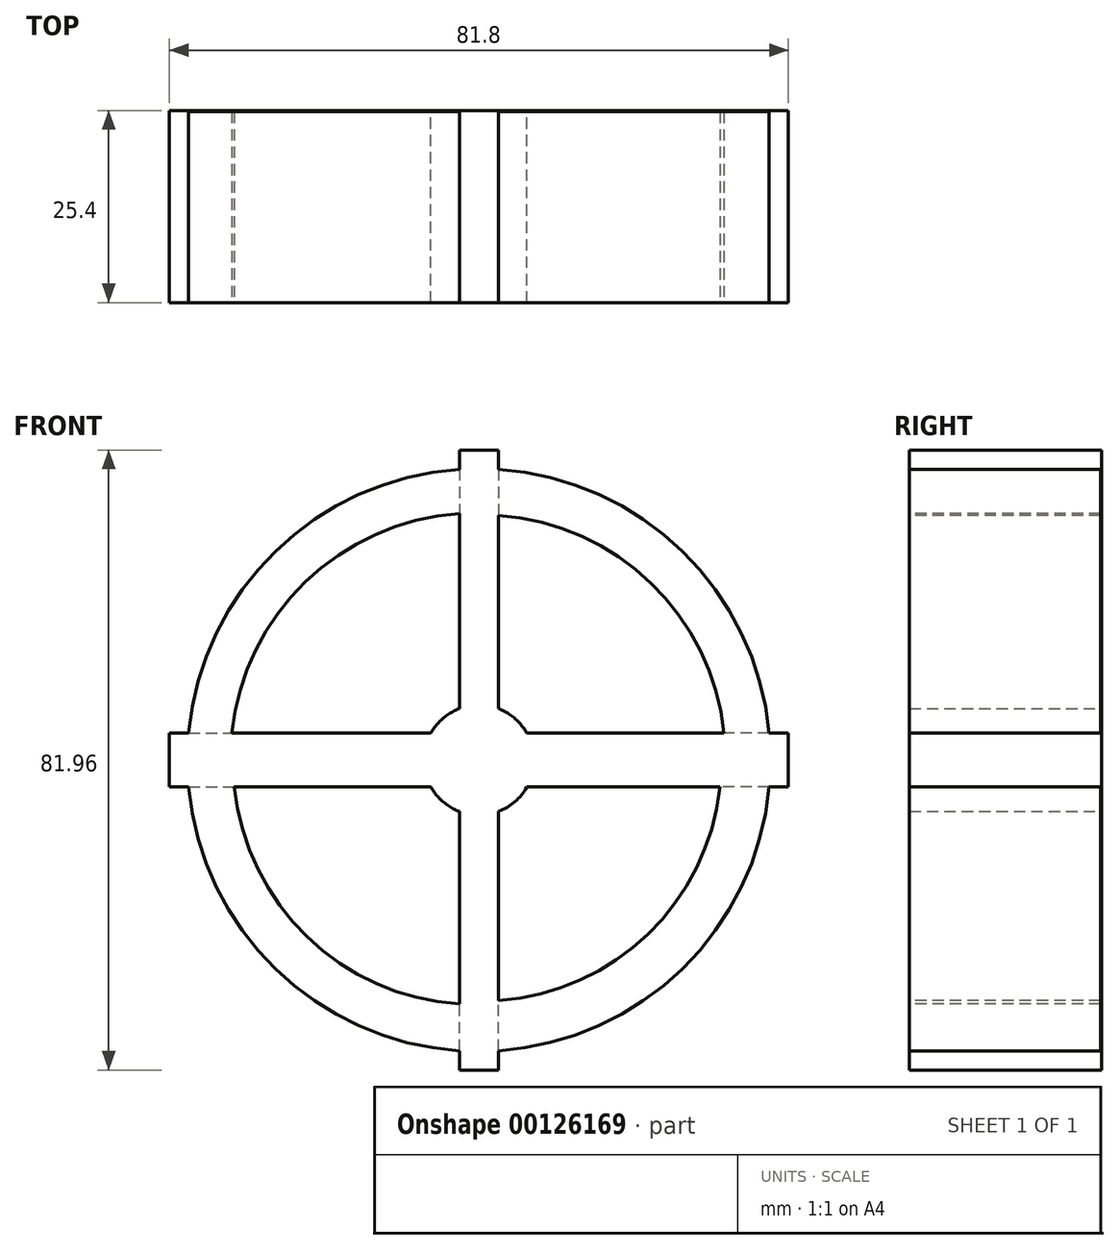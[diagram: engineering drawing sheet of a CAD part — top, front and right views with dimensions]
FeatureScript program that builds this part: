
annotation { "Feature Type Name" : "Feature", "Feature Type Description" : "" }
export const myFeature = defineFeature(function(context is Context, id is Id, definition is map)
    precondition{}
    {
        {
            var Q0;
            Q0=qCreatedBy(makeId("Front.planeOp"),FACE);
            var sketch = newSketch(context, id + "F0", { "sketchPlane" : qUnion([Q0])});
            skLineSegment(sketch, "E0", {"start": v(-2.58, -40.98) * mm, "end": v(-2.58, -40.98) * mm});
            skArc(sketch, "E1", {"start": v(-6.34, -3.57) * mm, "mid": v(-4.74, -5.52) * mm, "end": v(-2.58, -6.8) * mm});
            skLineSegment(sketch, "E2", {"start": v(-2.58, 40.98) * mm, "end": v(-2.58, 6.8) * mm});
            skLineSegment(sketch, "E3.MirrorCS", {"start": v(2.58, 40.98) * mm, "end": v(2.58, 6.8) * mm});
            skLineSegment(sketch, "E4.MirrorCS", {"start": v(-2.58, -40.98) * mm, "end": v(-2.58, -6.8) * mm});
            skLineSegment(sketch, "E5.MirrorCS", {"start": v(2.58, -40.98) * mm, "end": v(2.58, -6.8) * mm});
            skLineSegment(sketch, "E6", {"start": v(-40.9, -3.57) * mm, "end": v(-6.34, -3.57) * mm});
            skLineSegment(sketch, "E7.MirrorCS", {"start": v(-40.9, 3.57) * mm, "end": v(-6.34, 3.57) * mm});
            skLineSegment(sketch, "E8.MirrorCS", {"start": v(40.9, 3.57) * mm, "end": v(6.34, 3.57) * mm});
            skLineSegment(sketch, "E9.MirrorCS", {"start": v(40.9, -3.57) * mm, "end": v(6.34, -3.57) * mm});
            skLineSegment(sketch, "E10.left", {"start": v(-40.9, 3.57) * mm, "end": v(-40.9, -3.57) * mm});
            skLineSegment(sketch, "E10.right", {"start": v(-6.34, 3.57) * mm, "end": v(-6.34, -3.57) * mm});
            skLineSegment(sketch, "E11.bottom", {"start": v(-2.58, 40.98) * mm, "end": v(2.58, 40.98) * mm});
            skLineSegment(sketch, "E11.top", {"start": v(-2.58, 40.98) * mm, "end": v(2.58, 40.98) * mm});
            skLineSegment(sketch, "E11.left", {"start": v(-2.58, 40.98) * mm, "end": v(-2.58, 40.98) * mm});
            skLineSegment(sketch, "E11.right", {"start": v(2.58, 40.98) * mm, "end": v(2.58, 40.98) * mm});
            skLineSegment(sketch, "E12.top", {"start": v(-2.58, 6.8) * mm, "end": v(2.58, 6.8) * mm});
            skArc(sketch, "E13.trimOffspring", {"start": v(-2.58, 6.8) * mm, "mid": v(-4.74, 5.52) * mm, "end": v(-6.34, 3.57) * mm});
            skLineSegment(sketch, "E14.bottom", {"start": v(6.34, 3.57) * mm, "end": v(40.9, 3.57) * mm});
            skLineSegment(sketch, "E14.top", {"start": v(6.34, -3.57) * mm, "end": v(40.9, -3.57) * mm});
            skLineSegment(sketch, "E14.left", {"start": v(6.34, 3.57) * mm, "end": v(6.34, -3.57) * mm});
            skLineSegment(sketch, "E14.right", {"start": v(40.9, 3.57) * mm, "end": v(40.9, -3.57) * mm});
            skArc(sketch, "E15.trimOffspring", {"start": v(6.34, 3.57) * mm, "mid": v(4.74, 5.52) * mm, "end": v(2.58, 6.8) * mm});
            skLineSegment(sketch, "E16.bottom", {"start": v(-2.58, -6.8) * mm, "end": v(2.58, -6.8) * mm});
            skLineSegment(sketch, "E16.top", {"start": v(-2.58, -40.98) * mm, "end": v(2.58, -40.98) * mm});
            skLineSegment(sketch, "E16.left", {"start": v(-2.58, -6.8) * mm, "end": v(-2.58, -40.98) * mm});
            skLineSegment(sketch, "E16.right", {"start": v(2.58, -6.8) * mm, "end": v(2.58, -40.98) * mm});
            skArc(sketch, "E17.trimOffspring", {"start": v(2.58, -40.98) * mm, "mid": v(2.58, -40.98) * mm, "end": v(2.58, -40.98) * mm});
            skArc(sketch, "E18.trimOffspring", {"start": v(2.58, -6.8) * mm, "mid": v(4.74, -5.52) * mm, "end": v(6.34, -3.57) * mm});
            skSolve(sketch);
        }
        {
            var Q0;
            Q0 = qSketchRegion(id + "F0", true);
            extrude(context, id + "F1", {"entities" : qUnion([Q0]), "depth" : 25.4 * mm});
        }
        {
            var Q0;
            Q0=makeQuery(id+"F1.opExtrude","CAP_FACE",FACE,{"disambiguationData":[OSD([sQuery(id+"F0.wireOp",EDGE,"E1"),sQuery(id+"F0.wireOp",EDGE,"E7.MirrorCS"),sQuery(id+"F0.wireOp",EDGE,"E6"),sQuery(id+"F0.wireOp",EDGE,"E10.left"),sQuery(id+"F0.wireOp",EDGE,"E11.bottom"),sQuery(id+"F0.wireOp",EDGE,"E2"),sQuery(id+"F0.wireOp",EDGE,"E3.MirrorCS"),sQuery(id+"F0.wireOp",EDGE,"E13.trimOffspring"),sQuery(id+"F0.wireOp",EDGE,"E14.bottom"),sQuery(id+"F0.wireOp",EDGE,"E14.top"),sQuery(id+"F0.wireOp",EDGE,"E14.right"),sQuery(id+"F0.wireOp",EDGE,"E15.trimOffspring"),sQuery(id+"F0.wireOp",EDGE,"E16.bottom"),sQuery(id+"F0.wireOp",EDGE,"E16.top"),sQuery(id+"F0.wireOp",EDGE,"E16.left"),sQuery(id+"F0.wireOp",EDGE,"E16.right"),sQuery(id+"F0.wireOp",EDGE,"E18.trimOffspring")])],"isStart":false});
            var sketch = newSketch(context, id + "F2", { "sketchPlane" : qUnion([Q0])});
            skLineSegment(sketch, "E19", {"start": v(-40.9, 3.57) * mm, "end": v(-6.34, 3.57) * mm});
            skLineSegment(sketch, "E20", {"start": v(-2.58, 6.8) * mm, "end": v(-2.58, 40.98) * mm});
            skArc(sketch, "E21", {"start": v(-2.58, 6.8) * mm, "mid": v(-4.74, 5.51) * mm, "end": v(-6.34, 3.57) * mm});
            skLineSegment(sketch, "E22", {"start": v(2.58, 6.8) * mm, "end": v(2.58, 40.98) * mm});
            skLineSegment(sketch, "E23", {"start": v(6.34, 3.57) * mm, "end": v(40.9, 3.57) * mm});
            skArc(sketch, "E24", {"start": v(6.34, 3.57) * mm, "mid": v(4.74, 5.51) * mm, "end": v(2.58, 6.8) * mm});
            skLineSegment(sketch, "E25.MirrorCS", {"start": v(-2.58, -6.8) * mm, "end": v(-2.58, -40.98) * mm});
            skArc(sketch, "E26.MirrorCS", {"start": v(-2.58, -6.8) * mm, "mid": v(-4.74, -5.51) * mm, "end": v(-6.34, -3.57) * mm});
            skLineSegment(sketch, "E27.MirrorCS", {"start": v(-40.9, -3.57) * mm, "end": v(-6.34, -3.57) * mm});
            skCircle(sketch, "E28.MirrorC", {"center": v(0, 0) * mm, "radius": 38.53 * mm});
            skArc(sketch, "E29.MirrorCS", {"start": v(-2.58, -32.27) * mm, "mid": v(-22.7, -23.36) * mm, "end": v(-32.32, -3.57) * mm});
            skArc(sketch, "E30.MirrorCS", {"start": v(6.34, -3.57) * mm, "mid": v(4.74, -5.51) * mm, "end": v(2.58, -6.8) * mm});
            skLineSegment(sketch, "E31.MirrorCS", {"start": v(2.58, -6.8) * mm, "end": v(2.58, -40.98) * mm});
            skLineSegment(sketch, "E32.MirrorCS", {"start": v(6.34, -3.57) * mm, "end": v(40.9, -3.57) * mm});
            skArc(sketch, "E33.MirrorCS", {"start": v(2.4, -31.8) * mm, "mid": v(22.4, -22.98) * mm, "end": v(31.87, -3.28) * mm});
            skArc(sketch, "E34.MirrorCS", {"start": v(-2.44, 32.59) * mm, "mid": v(-22.94, 23.54) * mm, "end": v(-32.65, 3.36) * mm});
            skArc(sketch, "E35.MirrorCS", {"start": v(2.43, 32.34) * mm, "mid": v(22.77, 23.37) * mm, "end": v(32.4, 3.33) * mm});
            skSolve(sketch);
        }
        {
            var Q0;
            Q0 = qSketchRegion(id + "F2", true);
            extrude(context, id + "F3", {"entities" : qUnion([Q0]), "operationType" : NewBodyOperationType.ADD, "oppositeDirection" : true, "depth" : 25.24 * mm});
        }
    });
